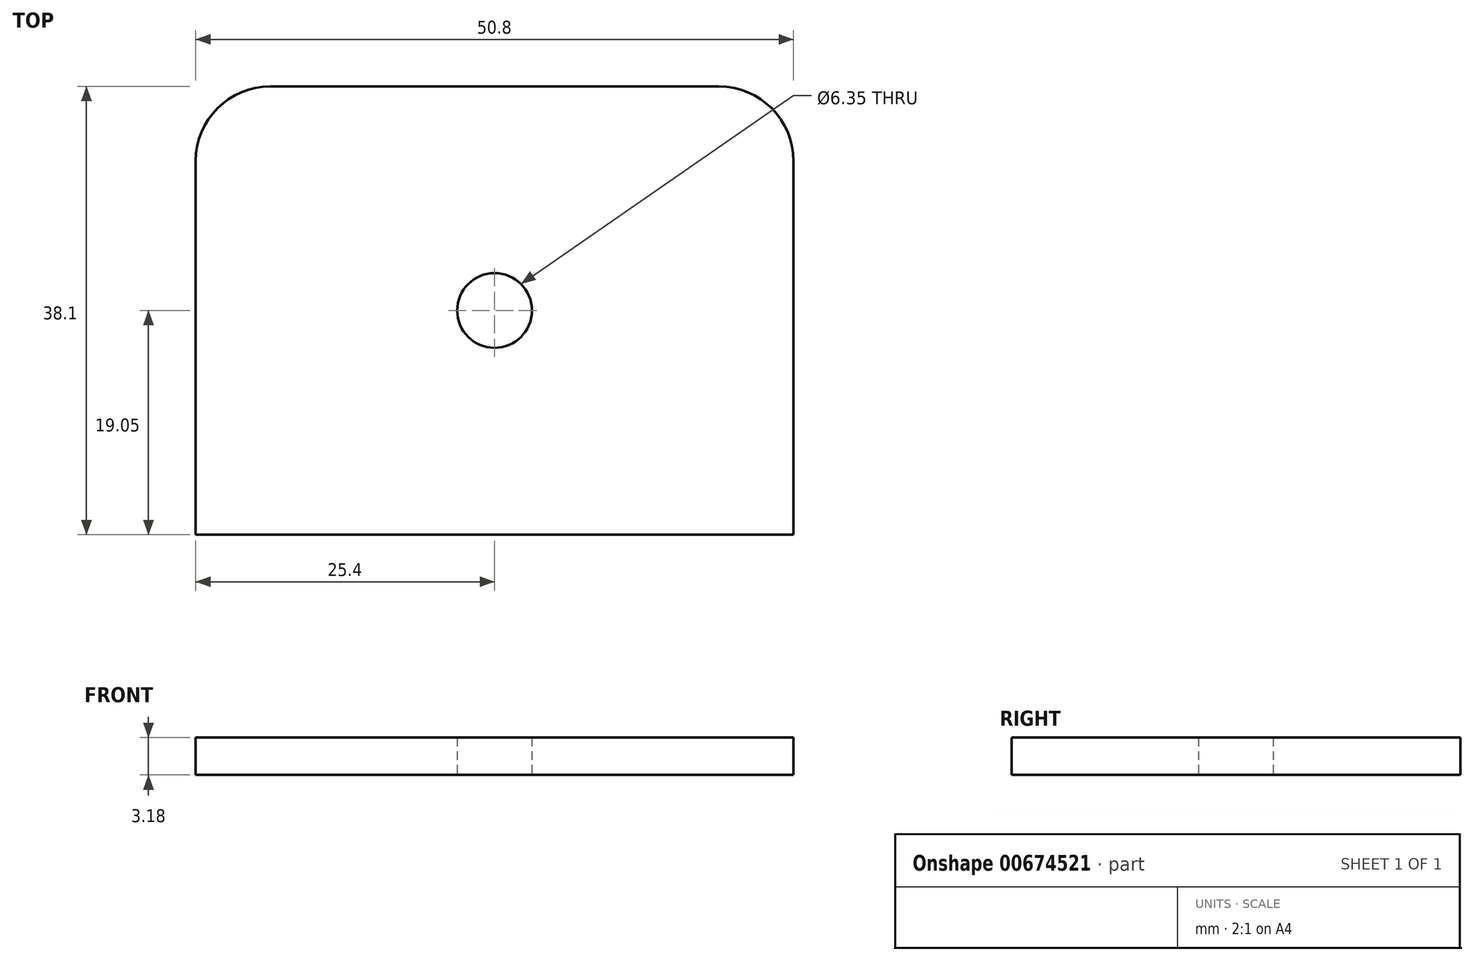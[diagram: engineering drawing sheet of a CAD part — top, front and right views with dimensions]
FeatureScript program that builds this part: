
annotation { "Feature Type Name" : "Feature", "Feature Type Description" : "" }
export const myFeature = defineFeature(function(context is Context, id is Id, definition is map)
    precondition{}
    {
        {
            var Q0;
            Q0=qCreatedBy(makeId("Top.planeOp"),FACE);
            var sketch = newSketch(context, id + "F0", { "sketchPlane" : qUnion([Q0])});
            skLineSegment(sketch, "E0.bottom", {"start": v(19.05, 19.05) * mm, "end": v(-19.05, 19.05) * mm});
            skLineSegment(sketch, "E0.top", {"start": v(25.4, -19.05) * mm, "end": v(-25.4, -19.05) * mm});
            skLineSegment(sketch, "E0.left", {"start": v(25.4, 12.7) * mm, "end": v(25.4, -19.05) * mm});
            skLineSegment(sketch, "E0.right", {"start": v(-25.4, 12.7) * mm, "end": v(-25.4, -19.05) * mm});
            skPoint(sketch, "E0.middle", {"position": v(0, 0) * mm});
            skCircle(sketch, "E1", {"center": v(0, 0) * mm, "radius": 3.18 * mm});
            skPoint(sketch, "E2.visualSharp", {"position": v(25.4, 19.05) * mm});
            skArc(sketch, "E2.filletArc", {"start": v(25.4, 12.7) * mm, "mid": v(23.54, 17.2) * mm, "end": v(19.05, 19.05) * mm});
            skPoint(sketch, "E3.visualSharp", {"position": v(-25.4, 19.05) * mm});
            skArc(sketch, "E3.filletArc", {"start": v(-19.05, 19.05) * mm, "mid": v(-23.54, 17.2) * mm, "end": v(-25.4, 12.7) * mm});
            skSolve(sketch);
        }
        {
            var Q0;
            Q0 = qSketchRegion(id + "F0", true);
            extrude(context, id + "F1", {"entities" : qUnion([Q0]), "depth" : 3.17 * mm, "offsetDistance" : 25.4 * mm});
        }
    });
